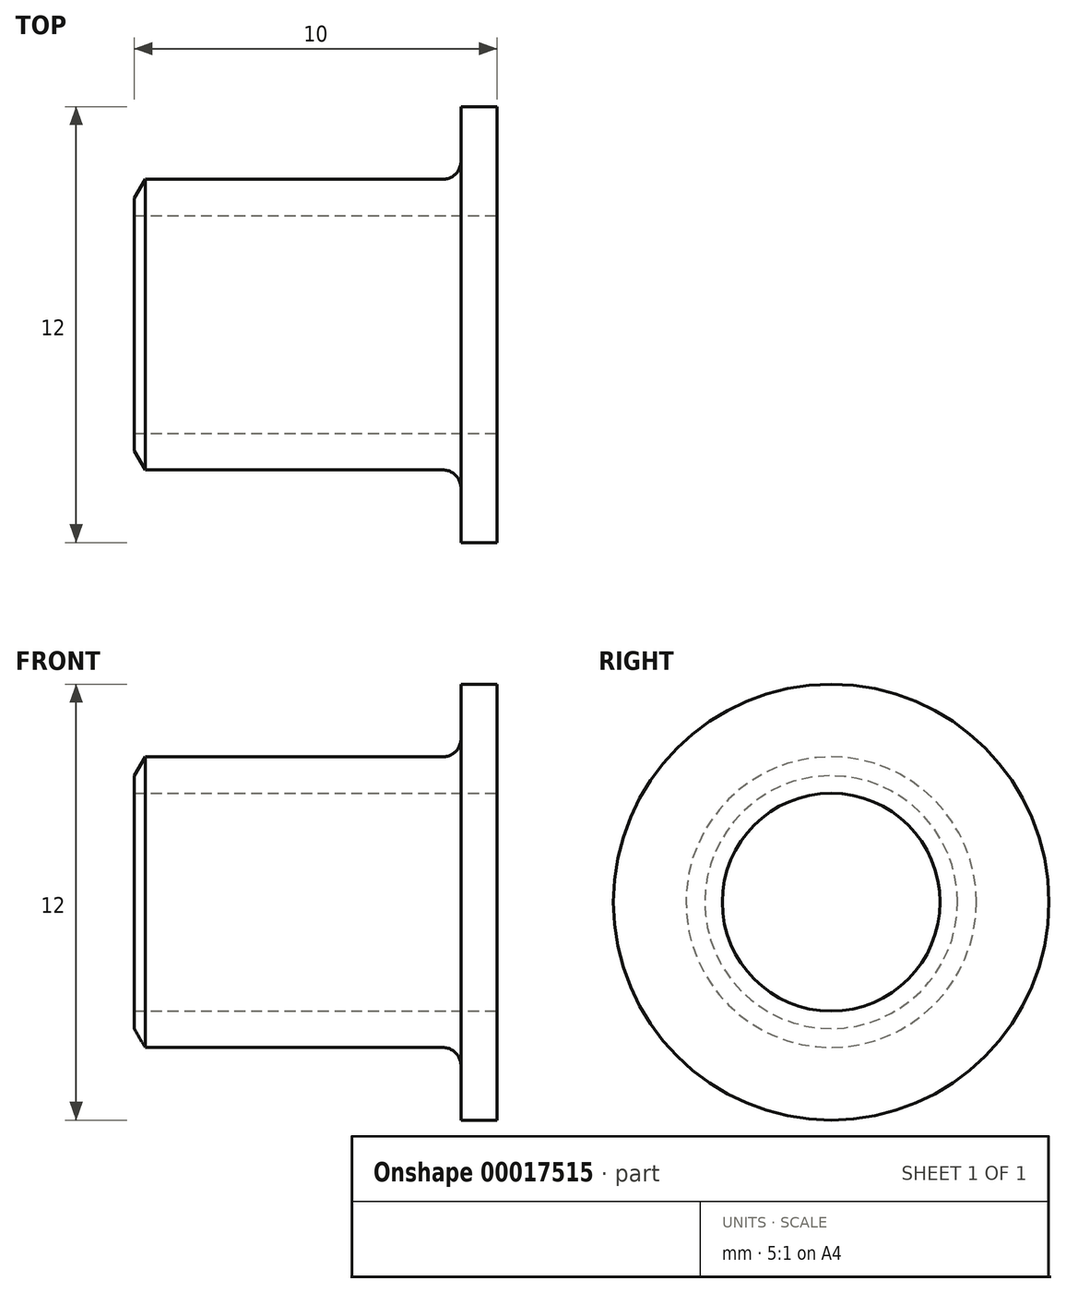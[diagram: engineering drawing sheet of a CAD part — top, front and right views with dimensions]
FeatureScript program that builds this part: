
annotation { "Feature Type Name" : "Feature", "Feature Type Description" : "" }
export const myFeature = defineFeature(function(context is Context, id is Id, definition is map)
    precondition{}
    {
        {
            var Q0;
            Q0=qCreatedBy(makeId("Front.planeOp"),FACE);
            var sketch = newSketch(context, id + "F0", { "sketchPlane" : qUnion([Q0])});
            skLineSegment(sketch, "E0", {"start": v(1, 0) * mm, "end": v(-9, 0) * mm, "construction": true});
            skLineSegment(sketch, "E1", {"start": v(1, 3) * mm, "end": v(-9, 3) * mm});
            skLineSegment(sketch, "E2", {"start": v(-9, 3) * mm, "end": v(-9, 3.48) * mm});
            skLineSegment(sketch, "E3", {"start": v(-9, 3.48) * mm, "end": v(-8.7, 4) * mm});
            skLineSegment(sketch, "E4", {"start": v(-8.7, 4) * mm, "end": v(-0.5, 4) * mm});
            skLineSegment(sketch, "E5", {"start": v(0, 4.5) * mm, "end": v(0, 6) * mm});
            skLineSegment(sketch, "E6", {"start": v(0, 6) * mm, "end": v(1, 6) * mm});
            skLineSegment(sketch, "E7", {"start": v(1, 6) * mm, "end": v(1, 3) * mm});
            skArc(sketch, "E8.filletArc", {"start": v(-0.5, 4) * mm, "mid": v(-0.15, 4.15) * mm, "end": v(0, 4.5) * mm});
            skSolve(sketch);
        }
        {
            var Q0;
            Q0 = qSketchRegion(id + "F0", true);
            var Q1;
            Q1=sQuery(id+"F0.wireOp",EDGE,"E0");
            revolve(context, id + "F1", {"entities" : qUnion([Q0]), "axis" : qUnion([Q1]), "revolveType" : RevolveType.FULL});
        }
    });
